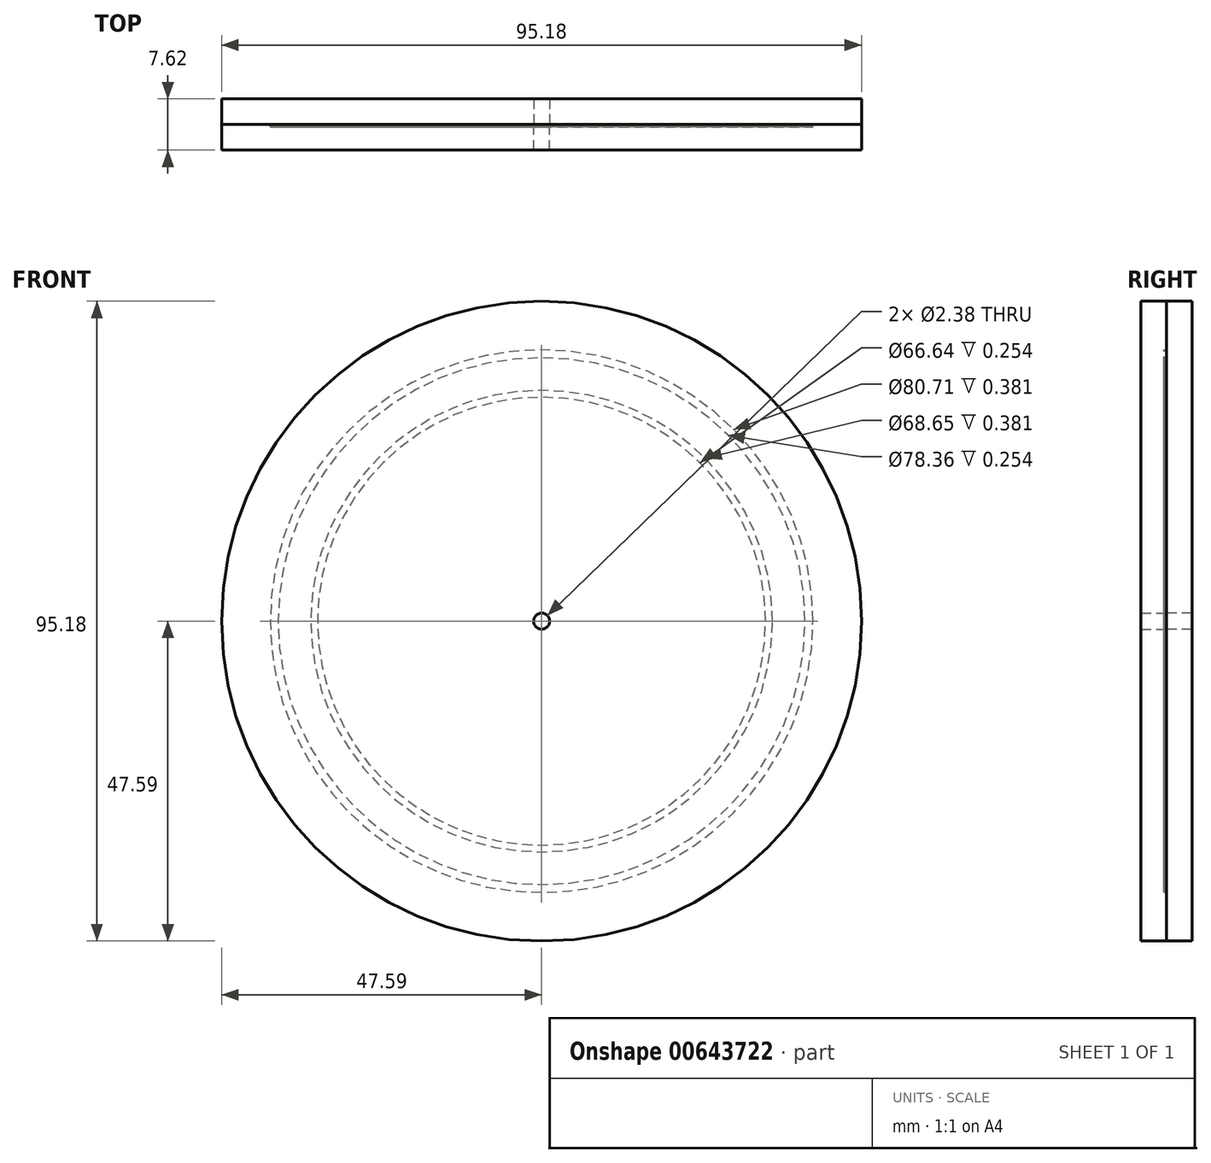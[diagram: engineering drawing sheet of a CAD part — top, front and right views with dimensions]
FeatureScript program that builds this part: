
annotation { "Feature Type Name" : "Feature", "Feature Type Description" : "" }
export const myFeature = defineFeature(function(context is Context, id is Id, definition is map)
    precondition{}
    {
        {
            var Q0;
            Q0=qCreatedBy(makeId("Front.planeOp"),FACE);
            var sketch = newSketch(context, id + "F0", { "sketchPlane" : qUnion([Q0])});
            skCircle(sketch, "E0", {"center": v(0, 0) * mm, "radius": 47.6 * mm});
            skCircle(sketch, "E1", {"center": v(0, 0) * mm, "radius": 1.2 * mm});
            skCircle(sketch, "E2", {"center": v(0, 0) * mm, "radius": 40.36 * mm});
            skCircle(sketch, "E3", {"center": v(0, 0) * mm, "radius": 39.18 * mm});
            skCircle(sketch, "E4", {"center": v(0, 0) * mm, "radius": 34.33 * mm});
            skCircle(sketch, "E5", {"center": v(0, 0) * mm, "radius": 33.32 * mm});
            skSolve(sketch);
        }
        {
            var Q0;
            Q0=makeQuery(id+"F0.imprint","IMPRINT",FACE,{"disambiguationData":[TD([[makeQuery(id+"F0.imprint","IMPRINT",EDGE,{"derivedFrom":sQuery(id+"F0.wireOp",EDGE,"E2")}),1.0]])]});
            var Q1;
            Q1=makeQuery(id+"F0.imprint","IMPRINT",FACE,{"disambiguationData":[TD([[makeQuery(id+"F0.imprint","IMPRINT",EDGE,{"derivedFrom":sQuery(id+"F0.wireOp",EDGE,"E4")}),1.0]])]});
            extrude(context, id + "F1", {"entities" : qUnion([Q0, Q1]), "depth" : 0.25 * mm, "offsetDistance" : 25.4 * mm});
        }
        {
            var Q0;
            Q0=makeQuery(id+"F0.imprint","IMPRINT",FACE,{"disambiguationData":[TD([[makeQuery(id+"F0.imprint","IMPRINT",EDGE,{"derivedFrom":sQuery(id+"F0.wireOp",EDGE,"E0")}),1.0]])]});
            var Q1;
            Q1=makeQuery(id+"F0.imprint","IMPRINT",FACE,{"disambiguationData":[TD([[makeQuery(id+"F0.imprint","IMPRINT",EDGE,{"derivedFrom":sQuery(id+"F0.wireOp",EDGE,"E2")}),1.0]])]});
            var Q2;
            Q2=makeQuery(id+"F0.imprint","IMPRINT",FACE,{"disambiguationData":[TD([[makeQuery(id+"F0.imprint","IMPRINT",EDGE,{"derivedFrom":sQuery(id+"F0.wireOp",EDGE,"E3")}),1.0]])]});
            var Q3;
            Q3=makeQuery(id+"F0.imprint","IMPRINT",FACE,{"disambiguationData":[TD([[makeQuery(id+"F0.imprint","IMPRINT",EDGE,{"derivedFrom":sQuery(id+"F0.wireOp",EDGE,"E4")}),1.0]])]});
            var Q4;
            Q4=makeQuery(id+"F0.imprint","IMPRINT",FACE,{"disambiguationData":[TD([[makeQuery(id+"F0.imprint","IMPRINT",EDGE,{"derivedFrom":sQuery(id+"F0.wireOp",EDGE,"E1")}),-1.0]])]});
            extrude(context, id + "F2", {"entities" : qUnion([Q0, Q1, Q2, Q3, Q4]), "oppositeDirection" : true, "depth" : 3.8 * mm, "offsetDistance" : 25.4 * mm});
        }
        {
            var Q0;
            Q0=makeQuery(id+"F0.imprint","IMPRINT",FACE,{"disambiguationData":[TD([[makeQuery(id+"F0.imprint","IMPRINT",EDGE,{"derivedFrom":sQuery(id+"F0.wireOp",EDGE,"E2")}),1.0]])]});
            var Q1;
            Q1=makeQuery(id+"F0.imprint","IMPRINT",FACE,{"disambiguationData":[TD([[makeQuery(id+"F0.imprint","IMPRINT",EDGE,{"derivedFrom":sQuery(id+"F0.wireOp",EDGE,"E4")}),1.0]])]});
            var Q2;
            Q2=makeQuery(id+"F0.imprint","IMPRINT",FACE,{"disambiguationData":[TD([[makeQuery(id+"F0.imprint","IMPRINT",EDGE,{"derivedFrom":sQuery(id+"F0.wireOp",EDGE,"E0")}),1.0]])]});
            var Q3;
            Q3=makeQuery(id+"F0.imprint","IMPRINT",FACE,{"disambiguationData":[TD([[makeQuery(id+"F0.imprint","IMPRINT",EDGE,{"derivedFrom":sQuery(id+"F0.wireOp",EDGE,"E3")}),1.0]])]});
            var Q4;
            Q4=makeQuery(id+"F0.imprint","IMPRINT",FACE,{"disambiguationData":[TD([[makeQuery(id+"F0.imprint","IMPRINT",EDGE,{"derivedFrom":sQuery(id+"F0.wireOp",EDGE,"E1")}),-1.0]])]});
            extrude(context, id + "F3", {"entities" : qUnion([Q0, Q1, Q2, Q3, Q4]), "depth" : 3.8 * mm, "offsetDistance" : 25.4 * mm});
        }
        {
            var Q0;
            Q0=makeQuery(id+"F0.imprint","IMPRINT",FACE,{"disambiguationData":[TD([[makeQuery(id+"F0.imprint","IMPRINT",EDGE,{"derivedFrom":sQuery(id+"F0.wireOp",EDGE,"E2")}),1.0]])]});
            var Q1;
            Q1=makeQuery(id+"F0.imprint","IMPRINT",FACE,{"disambiguationData":[TD([[makeQuery(id+"F0.imprint","IMPRINT",EDGE,{"derivedFrom":sQuery(id+"F0.wireOp",EDGE,"E4")}),1.0]])]});
            extrude(context, id + "F4", {"entities" : qUnion([Q0, Q1]), "depth" : 0.38 * mm, "offsetDistance" : 25.4 * mm});
        }
        {
            var Q0;
            Q0=makeQuery(id+"F4.opExtrude","SWEPT_BODY",BODY,{"disambiguationData":[OSD([sQuery(id+"F0.wireOp",EDGE,"E2"),sQuery(id+"F0.wireOp",EDGE,"E3")])]});
            var Q1;
            Q1=makeQuery(id+"F3.opExtrude","SWEPT_BODY",BODY,{"disambiguationData":[OSD([sQuery(id+"F0.wireOp",EDGE,"E0"),sQuery(id+"F0.wireOp",EDGE,"E1")])]});
            booleanBodies(context, id + "F5", {"operationType" : BooleanOperationType.SUBTRACTION, "tools" : qUnion([Q0]), "targets" : qUnion([Q1])});
        }
        {
            var Q0;
            Q0=makeQuery(id+"F4.opExtrude","SWEPT_BODY",BODY,{"disambiguationData":[OSD([sQuery(id+"F0.wireOp",EDGE,"E4"),sQuery(id+"F0.wireOp",EDGE,"E5")])]});
            var Q1;
            Q1=makeQuery(id+"F3.opExtrude","SWEPT_BODY",BODY,{"disambiguationData":[OSD([sQuery(id+"F0.wireOp",EDGE,"E0"),sQuery(id+"F0.wireOp",EDGE,"E1")])]});
            booleanBodies(context, id + "F6", {"operationType" : BooleanOperationType.SUBTRACTION, "tools" : qUnion([Q0]), "targets" : qUnion([Q1])});
        }
    });
